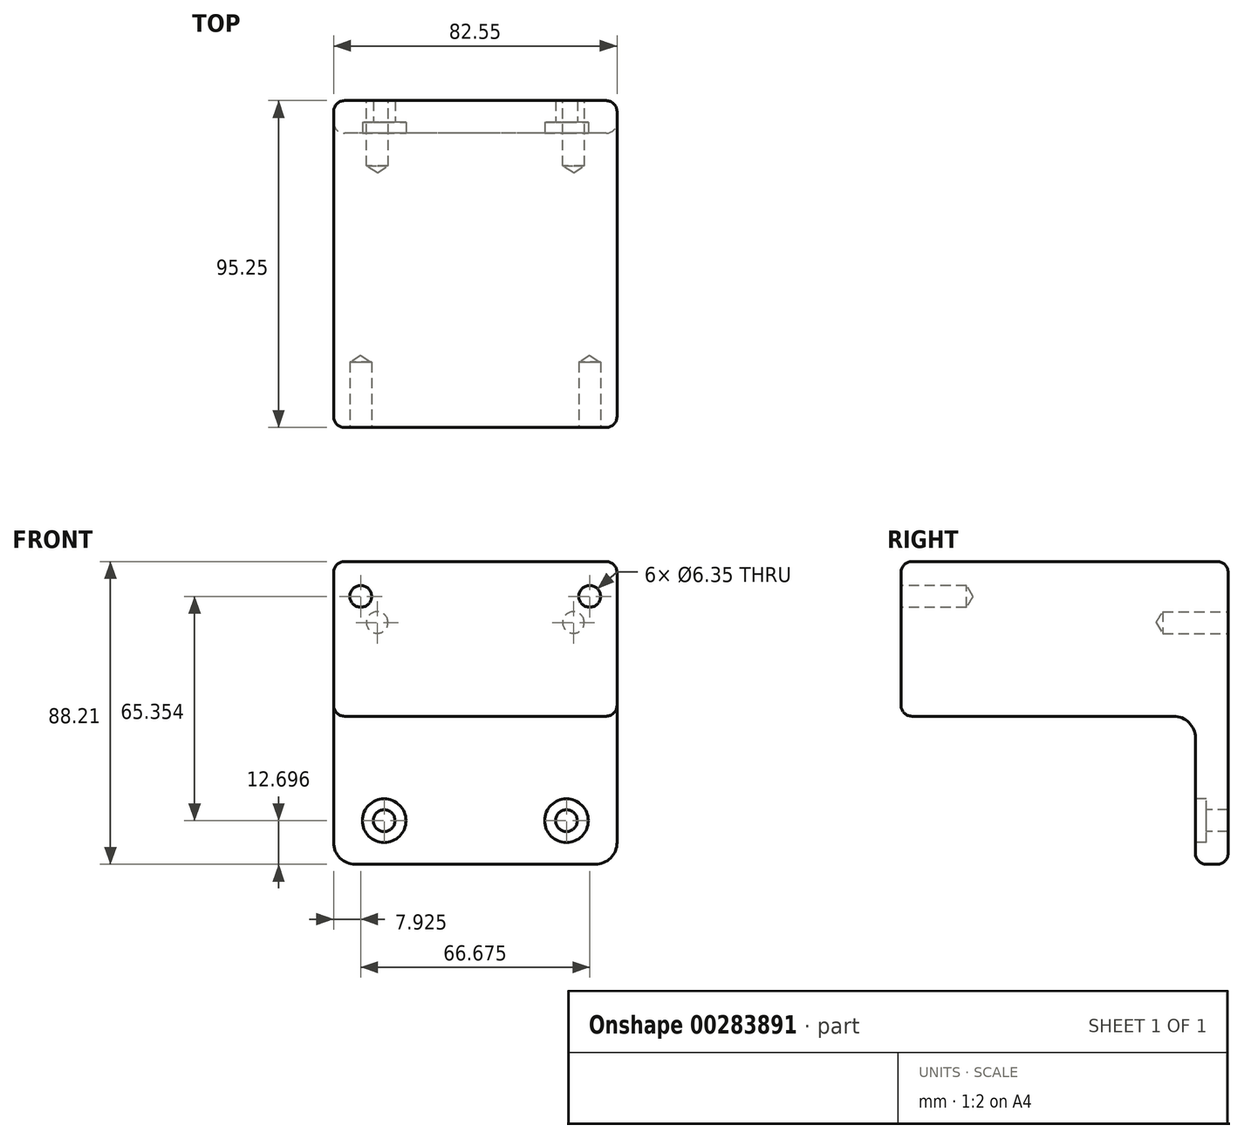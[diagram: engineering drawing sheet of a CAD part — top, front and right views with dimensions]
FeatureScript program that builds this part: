
annotation { "Feature Type Name" : "Feature", "Feature Type Description" : "" }
export const myFeature = defineFeature(function(context is Context, id is Id, definition is map)
    precondition{}
    {
        {
            var Q0;
            Q0=qCreatedBy(makeId("Front.planeOp"),FACE);
            var sketch = newSketch(context, id + "F0", { "sketchPlane" : qUnion([Q0])});
            skLineSegment(sketch, "E0.bottom", {"start": v(0, 0) * mm, "end": v(82.55, 0) * mm});
            skLineSegment(sketch, "E0.top", {"start": v(0, 35.56) * mm, "end": v(82.55, 35.56) * mm});
            skLineSegment(sketch, "E0.left", {"start": v(0, 0) * mm, "end": v(0, 35.56) * mm});
            skLineSegment(sketch, "E0.right", {"start": v(82.55, 0) * mm, "end": v(82.55, 35.56) * mm});
            skSolve(sketch);
        }
        {
            var Q0;
            Q0 = qSketchRegion(id + "F0", true);
            extrude(context, id + "F1", {"entities" : qUnion([Q0]), "depth" : 95.25 * mm});
        }
        {
            var Q0;
            Q0=makeQuery(id+"F1.opExtrude","CAP_FACE",FACE,{"disambiguationData":[OSD([sQuery(id+"F0.wireOp",EDGE,"E0.bottom"),sQuery(id+"F0.wireOp",EDGE,"E0.top"),sQuery(id+"F0.wireOp",EDGE,"E0.left"),sQuery(id+"F0.wireOp",EDGE,"E0.right")])],"isStart":false});
            var sketch = newSketch(context, id + "F2", { "sketchPlane" : qUnion([Q0])});
            skPoint(sketch, "E1", {"position": v(7.92, 25.4) * mm});
            skPoint(sketch, "E2", {"position": v(74.6, 25.4) * mm});
            skSolve(sketch);
        }
        {
            var Q0;
            Q0=sQuery(id+"F2.wireOp",VERTEX,"E1");
            var Q1;
            Q1=sQuery(id+"F2.wireOp",VERTEX,"E2");
            var Q2;
            Q2=makeQuery(id+"F1.opExtrude","SWEPT_BODY",BODY,{"disambiguationData":[OSD([sQuery(id+"F0.wireOp",EDGE,"E0.bottom"),sQuery(id+"F0.wireOp",EDGE,"E0.top"),sQuery(id+"F0.wireOp",EDGE,"E0.left"),sQuery(id+"F0.wireOp",EDGE,"E0.right")])]});
            hole(context, id + "F3", {"style" : HoleStyle.SIMPLE, "endStyle" : HoleEndStyle.BLIND, "holeDiameter" : 6.35 * mm, "holeDepth" : 19.05 * mm, "tappedDepth" : 12.7 * mm, "tapClearance" : 3, "locations" : qUnion([Q0, Q1]), "scope" : qUnion([Q2])});
        }
        {
            var Q0;
            Q0=makeQuery(id+"F1.opExtrude","CAP_FACE",FACE,{"disambiguationData":[OSD([sQuery(id+"F0.wireOp",EDGE,"E0.bottom"),sQuery(id+"F0.wireOp",EDGE,"E0.top"),sQuery(id+"F0.wireOp",EDGE,"E0.left"),sQuery(id+"F0.wireOp",EDGE,"E0.right")])],"isStart":true});
            var sketch = newSketch(context, id + "F4", { "sketchPlane" : qUnion([Q0])});
            skPoint(sketch, "E3", {"position": v(-69.85, 17.78) * mm});
            skPoint(sketch, "E3.positionSnap0", {"position": v(-82.55, 17.78) * mm});
            skPoint(sketch, "E4", {"position": v(-12.7, 17.78) * mm});
            skSolve(sketch);
        }
        {
            var Q0;
            Q0=sQuery(id+"F4.wireOp",VERTEX,"E4");
            var Q1;
            Q1=sQuery(id+"F4.wireOp",VERTEX,"E3");
            var Q2;
            Q2=makeQuery(id+"F1.opExtrude","SWEPT_BODY",BODY,{"disambiguationData":[OSD([sQuery(id+"F0.wireOp",EDGE,"E0.bottom"),sQuery(id+"F0.wireOp",EDGE,"E0.top"),sQuery(id+"F0.wireOp",EDGE,"E0.left"),sQuery(id+"F0.wireOp",EDGE,"E0.right")])]});
            hole(context, id + "F5", {"style" : HoleStyle.SIMPLE, "endStyle" : HoleEndStyle.BLIND, "holeDiameter" : 6.35 * mm, "holeDepth" : 19.05 * mm, "tappedDepth" : 12.7 * mm, "tapClearance" : 3, "locations" : qUnion([Q0, Q1]), "scope" : qUnion([Q2])});
        }
        {
            var Q0;
            Q0=qCreatedBy(makeId("Right.planeOp"),FACE);
            var sketch = newSketch(context, id + "F6", { "sketchPlane" : qUnion([Q0])});
            skLineSegment(sketch, "E5.bottom", {"start": v(0, 0) * mm, "end": v(-95.25, 0) * mm});
            skLineSegment(sketch, "E5.top", {"start": v(-15.87, -9.52) * mm, "end": v(-95.25, -9.53) * mm});
            skLineSegment(sketch, "E5.left", {"start": v(0, 0) * mm, "end": v(0, -9.53) * mm});
            skLineSegment(sketch, "E5.right", {"start": v(-95.25, 0) * mm, "end": v(-95.25, -9.53) * mm});
            skLineSegment(sketch, "E6.bottom", {"start": v(0, 0) * mm, "end": v(-9.53, 0) * mm});
            skLineSegment(sketch, "E6.top", {"start": v(0, -52.65) * mm, "end": v(-9.52, -52.65) * mm});
            skLineSegment(sketch, "E6.left", {"start": v(0, 0) * mm, "end": v(0, -52.65) * mm});
            skLineSegment(sketch, "E6.right", {"start": v(-9.52, -15.87) * mm, "end": v(-9.52, -52.65) * mm});
            skPoint(sketch, "E7.visualSharp", {"position": v(-9.52, -9.52) * mm});
            skArc(sketch, "E7.filletArc", {"start": v(-9.52, -15.87) * mm, "mid": v(-11.38, -11.38) * mm, "end": v(-15.87, -9.52) * mm});
            skSolve(sketch);
        }
        {
            var Q0;
            Q0 = qSketchRegion(id + "F6", true);
            extrude(context, id + "F7", {"entities" : qUnion([Q0]), "operationType" : NewBodyOperationType.ADD, "depth" : 82.55 * mm});
        }
        {
            var Q0;
            Q0=makeQuery(id+"F7.opExtrude","SWEPT_FACE",FACE,{"disambiguationData":[OSD([sQuery(id+"F6.wireOp",EDGE,"E6.right")])]});
            var sketch = newSketch(context, id + "F8", { "sketchPlane" : qUnion([Q0])});
            skPoint(sketch, "E8", {"position": v(14.73, -39.95) * mm});
            skPoint(sketch, "E9", {"position": v(67.82, -39.95) * mm});
            skSolve(sketch);
        }
        {
            var Q0;
            Q0=sQuery(id+"F8.wireOp",VERTEX,"E8");
            var Q1;
            Q1=sQuery(id+"F8.wireOp",VERTEX,"E9");
            var Q2;
            Q2=makeQuery(id+"F1.opExtrude","SWEPT_BODY",BODY,{"disambiguationData":[OSD([sQuery(id+"F0.wireOp",EDGE,"E0.bottom"),sQuery(id+"F0.wireOp",EDGE,"E0.top"),sQuery(id+"F0.wireOp",EDGE,"E0.left"),sQuery(id+"F0.wireOp",EDGE,"E0.right")])]});
            hole(context, id + "F9", {"style" : HoleStyle.C_BORE, "endStyle" : HoleEndStyle.THROUGH, "holeDiameter" : 6.35 * mm, "cBoreDiameter" : 12.7 * mm, "cBoreDepth" : 3.17 * mm, "tappedDepth" : 12.7 * mm, "tapClearance" : 3, "locations" : qUnion([Q0, Q1]), "scope" : qUnion([Q2])});
        }
        {
            var Q0;
            Q0=makeQuery(id+"F7.opExtrude","CAP_EDGE",EDGE,{"disambiguationData":[OSD([sQuery(id+"F6.wireOp",EDGE,"E6.top")])],"isStart":true});
            var Q1;
            Q1=makeQuery(id+"F7.opExtrude","CAP_EDGE",EDGE,{"disambiguationData":[OSD([sQuery(id+"F6.wireOp",EDGE,"E6.top")])],"isStart":false});
            fillet(context, id + "F10", {"entities" : qUnion([Q0, Q1]), "radius" : 6.35 * mm, "tangentPropagation" : true, "allowEdgeOverflow" : false});
        }
        {
            var Q0;
            Q0=makeQuery(id+"F7.boolean.opBoolean","MERGE",EDGE,{"derivedFrom":[makeQuery(id+"F1.opExtrude","CAP_EDGE",EDGE,{"disambiguationData":[OSD([sQuery(id+"F0.wireOp",EDGE,"E0.right")])],"isStart":false}),makeQuery(id+"F7.opExtrude","CAP_EDGE",EDGE,{"disambiguationData":[OSD([sQuery(id+"F6.wireOp",EDGE,"E5.right")])],"isStart":false})]});
            var Q1;
            Q1=makeQuery(id+"F7.opExtrude","SWEPT_EDGE",EDGE,{"disambiguationData":[OSD([sQuery(id+"F6.wireOp",EDGE,"E5.top"),sQuery(id+"F6.wireOp",EDGE,"E5.right")])]});
            var Q2;
            Q2=makeQuery(id+"F7.boolean.opBoolean","MERGE",EDGE,{"derivedFrom":[makeQuery(id+"F1.opExtrude","CAP_EDGE",EDGE,{"disambiguationData":[OSD([sQuery(id+"F0.wireOp",EDGE,"E0.left")])],"isStart":false}),makeQuery(id+"F7.opExtrude","CAP_EDGE",EDGE,{"disambiguationData":[OSD([sQuery(id+"F6.wireOp",EDGE,"E5.right")])],"isStart":true})]});
            var Q3;
            Q3=makeQuery(id+"F7.opExtrude","CAP_EDGE",EDGE,{"disambiguationData":[OSD([sQuery(id+"F6.wireOp",EDGE,"E5.top")])],"isStart":true});
            var Q4;
            Q4=makeQuery(id+"F1.opExtrude","SWEPT_EDGE",EDGE,{"disambiguationData":[OSD([sQuery(id+"F0.wireOp",EDGE,"E0.top"),sQuery(id+"F0.wireOp",EDGE,"E0.right")])]});
            var Q5;
            Q5=makeQuery(id+"F1.opExtrude","CAP_EDGE",EDGE,{"disambiguationData":[OSD([sQuery(id+"F0.wireOp",EDGE,"E0.top")])],"isStart":false});
            var Q6;
            Q6=makeQuery(id+"F1.opExtrude","SWEPT_EDGE",EDGE,{"disambiguationData":[OSD([sQuery(id+"F0.wireOp",EDGE,"E0.top"),sQuery(id+"F0.wireOp",EDGE,"E0.left")])]});
            var Q7;
            Q7=makeQuery(id+"F1.opExtrude","CAP_EDGE",EDGE,{"disambiguationData":[OSD([sQuery(id+"F0.wireOp",EDGE,"E0.top")])],"isStart":true});
            var Q8;
            Q8=makeQuery(id+"F7.boolean.opBoolean","MERGE",EDGE,{"derivedFrom":[makeQuery(id+"F1.opExtrude","CAP_EDGE",EDGE,{"disambiguationData":[OSD([sQuery(id+"F0.wireOp",EDGE,"E0.left")])],"isStart":true}),makeQuery(id+"F7.opExtrude","CAP_EDGE",EDGE,{"disambiguationData":[OSD([sQuery(id+"F6.wireOp",EDGE,"E6.left")])],"isStart":true})]});
            fillet(context, id + "F11", {"entities" : qUnion([Q0, Q1, Q2, Q3, Q4, Q5, Q6, Q7, Q8]), "radius" : 3.17 * mm, "tangentPropagation" : true, "allowEdgeOverflow" : false});
        }
    });
